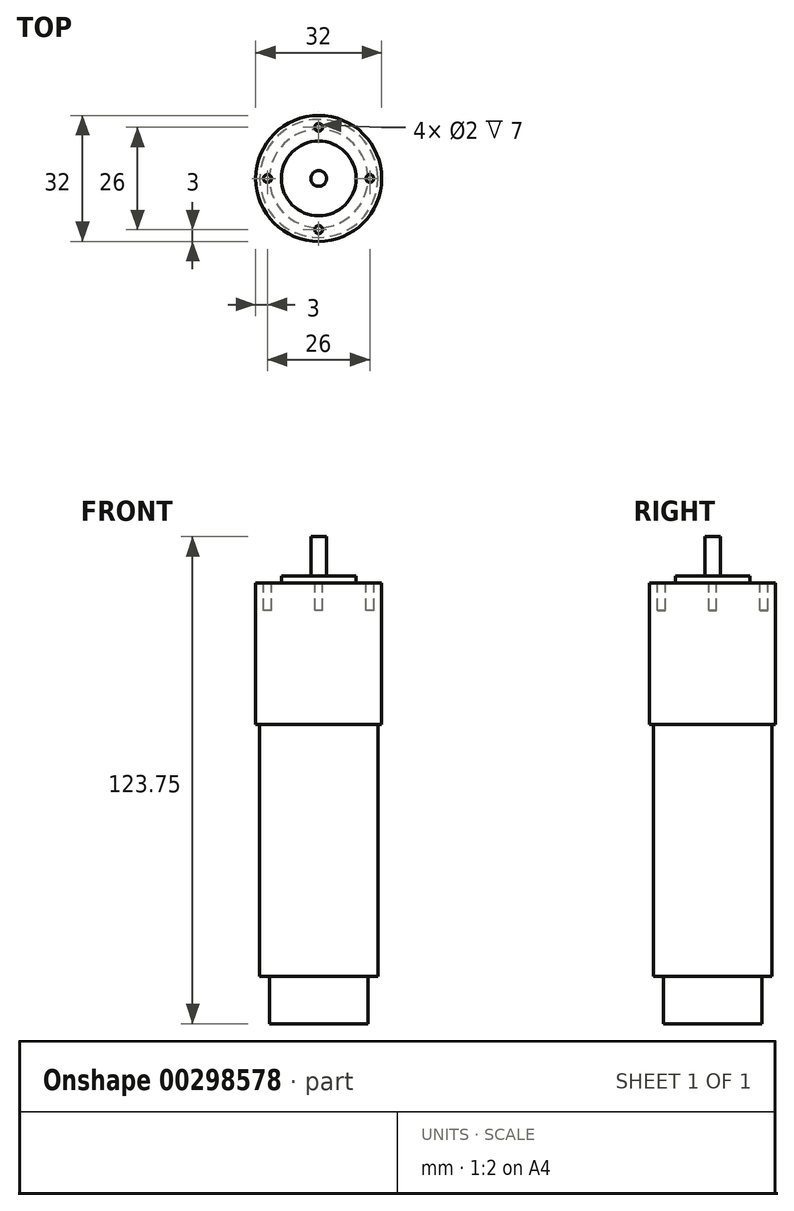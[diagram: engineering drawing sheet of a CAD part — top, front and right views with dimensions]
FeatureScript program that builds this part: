
annotation { "Feature Type Name" : "Feature", "Feature Type Description" : "" }
export const myFeature = defineFeature(function(context is Context, id is Id, definition is map)
    precondition{}
    {
        {
            var Q0;
            Q0=qCreatedBy(makeId("Front.planeOp"),FACE);
            var sketch = newSketch(context, id + "F0", { "sketchPlane" : qUnion([Q0])});
            skLineSegment(sketch, "E0", {"start": v(0, 0) * mm, "end": v(0, 140.73) * mm, "construction": true});
            skLineSegment(sketch, "E1", {"start": v(0, 123.75) * mm, "end": v(2, 123.75) * mm});
            skLineSegment(sketch, "E2", {"start": v(2, 123.75) * mm, "end": v(2, 113.75) * mm});
            skLineSegment(sketch, "E3", {"start": v(2, 113.75) * mm, "end": v(9.5, 113.75) * mm});
            skLineSegment(sketch, "E4", {"start": v(9.5, 113.75) * mm, "end": v(9.5, 112) * mm});
            skLineSegment(sketch, "E5", {"start": v(9.5, 112) * mm, "end": v(16, 112) * mm});
            skLineSegment(sketch, "E6", {"start": v(15, 76) * mm, "end": v(15, 12) * mm});
            skLineSegment(sketch, "E7", {"start": v(15, 12) * mm, "end": v(12.5, 12) * mm});
            skLineSegment(sketch, "E8", {"start": v(12.5, 12) * mm, "end": v(12.5, 0) * mm});
            skLineSegment(sketch, "E9", {"start": v(12.5, 0) * mm, "end": v(0, 0) * mm});
            skLineSegment(sketch, "E10", {"start": v(0, 123.75) * mm, "end": v(0, 0) * mm});
            skLineSegment(sketch, "E11", {"start": v(15, 76) * mm, "end": v(16, 76) * mm});
            skLineSegment(sketch, "E12", {"start": v(16, 76) * mm, "end": v(16, 112) * mm});
            skSolve(sketch);
        }
        {
            var Q0;
            Q0=qSketchRegion(id+"F0",true);
            var Q1;
            Q1=sQuery(id+"F0.wireOp",EDGE,"E0");
            revolve(context, id + "F1", {"entities" : qUnion([Q0]), "axis" : qUnion([Q1]), "revolveType" : RevolveType.FULL});
        }
        {
            var Q0;
            Q0=makeQuery(id+"F1.opRevolve","SWEPT_FACE",FACE,{"disambiguationData":[OSD([sQuery(id+"F0.wireOp",EDGE,"E5")])]});
            var sketch = newSketch(context, id + "F2", { "sketchPlane" : qUnion([Q0])});
            skCircle(sketch, "E13", {"center": v(0, 0) * mm, "radius": 13 * mm, "construction": true});
            skCircle(sketch, "E14", {"center": v(0, 13) * mm, "radius": 1 * mm});
            skCircle(sketch, "E15", {"center": v(13, 0) * mm, "radius": 1 * mm});
            skCircle(sketch, "E16", {"center": v(-13, 0) * mm, "radius": 1 * mm});
            skLineSegment(sketch, "E17", {"start": v(0, 0) * mm, "end": v(0, 13) * mm, "construction": true});
            skLineSegment(sketch, "E18", {"start": v(0, 0) * mm, "end": v(13, 0) * mm, "construction": true});
            skCircle(sketch, "E19.MirrorC", {"center": v(0, -13) * mm, "radius": 1 * mm});
            skSolve(sketch);
        }
        {
            var Q0;
            Q0=qSketchRegion(id+"F2",true);
            extrude(context, id + "F3", {"entities" : qUnion([Q0]), "operationType" : NewBodyOperationType.REMOVE, "oppositeDirection" : true, "depth" : 7 * mm});
        }
    });
